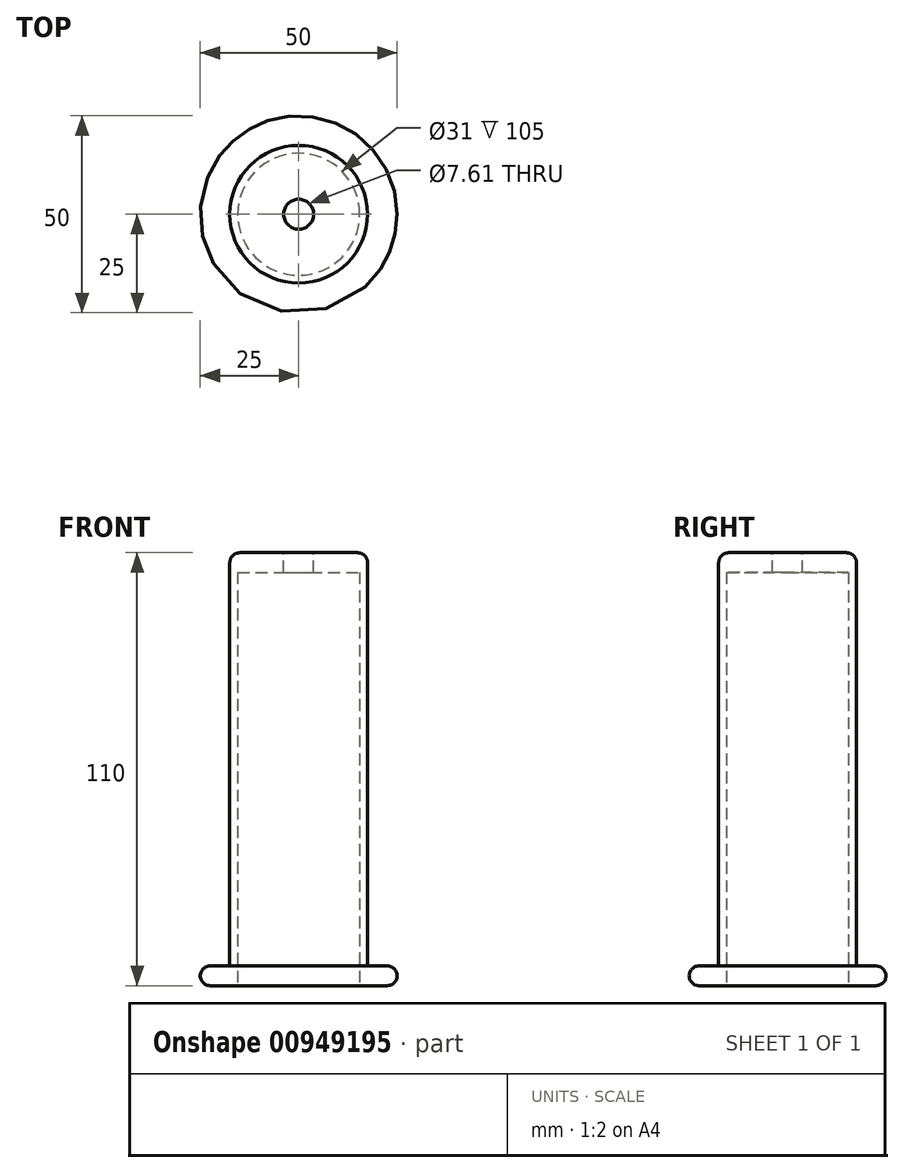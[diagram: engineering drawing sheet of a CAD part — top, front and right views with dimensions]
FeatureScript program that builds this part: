
annotation { "Feature Type Name" : "Feature", "Feature Type Description" : "" }
export const myFeature = defineFeature(function(context is Context, id is Id, definition is map)
    precondition{}
    {
        {
            var Q0;
            Q0=qCreatedBy(makeId("Top.planeOp"),FACE);
            var sketch = newSketch(context, id + "F0", { "sketchPlane" : qUnion([Q0])});
            skCircle(sketch, "E0", {"center": v(0, 0) * mm, "radius": 25 * mm});
            skSolve(sketch);
        }
        {
            var Q0;
            Q0 = qSketchRegion(id + "F0", true);
            var Q1;
            Q1=makeQuery(id+"F0.imprint","IMPRINT",FACE,{"disambiguationData":[TD([[makeQuery(id+"F0.imprint","IMPRINT",EDGE,{"derivedFrom":sQuery(id+"F0.wireOp",EDGE,"E0")}),1.0]])]});
            extrude(context, id + "F1", {"entities" : qUnion([Q0, Q1]), "depth" : 5 * mm, "offsetDistance" : 25 * mm});
        }
        {
            var Q0;
            Q0=makeQuery(id+"F1.opExtrude","CAP_FACE",FACE,{"disambiguationData":[OSD([sQuery(id+"F0.wireOp",EDGE,"E0")])],"isStart":false});
            var sketch = newSketch(context, id + "F2", { "sketchPlane" : qUnion([Q0])});
            skCircle(sketch, "E1", {"center": v(0, 0) * mm, "radius": 17.5 * mm});
            skSolve(sketch);
        }
        {
            var Q0;
            Q0 = qSketchRegion(id + "F2", true);
            var Q1;
            Q1=makeQuery(id+"F2.imprint","IMPRINT",FACE,{"disambiguationData":[TD([[makeQuery(id+"F2.imprint","IMPRINT",EDGE,{"derivedFrom":sQuery(id+"F2.wireOp",EDGE,"E1")}),1.0]])]});
            extrude(context, id + "F3", {"entities" : qUnion([Q0, Q1]), "operationType" : NewBodyOperationType.ADD, "depth" : 105 * mm, "offsetDistance" : 25 * mm});
        }
        {
            var Q0;
            Q0=makeQuery(id+"F1.opExtrude","CAP_FACE",FACE,{"disambiguationData":[OSD([sQuery(id+"F0.wireOp",EDGE,"E0")])],"isStart":true});
            var sketch = newSketch(context, id + "F4", { "sketchPlane" : qUnion([Q0])});
            skCircle(sketch, "E2", {"center": v(0, 0) * mm, "radius": 15.5 * mm});
            skSolve(sketch);
        }
        {
            var Q0;
            Q0=makeQuery(id+"F4.imprint","IMPRINT",FACE,{"disambiguationData":[TD([[makeQuery(id+"F4.imprint","IMPRINT",EDGE,{"derivedFrom":sQuery(id+"F4.wireOp",EDGE,"E2")}),1.0]])]});
            extrude(context, id + "F5", {"entities" : qUnion([Q0]), "operationType" : NewBodyOperationType.REMOVE, "oppositeDirection" : true, "depth" : 105 * mm, "offsetDistance" : 25 * mm});
        }
        {
            var Q0;
            Q0=makeQuery(id+"F3.opExtrude","CAP_EDGE",EDGE,{"disambiguationData":[OSD([sQuery(id+"F2.wireOp",EDGE,"E1")])],"isStart":false});
            var Q1;
            Q1=makeQuery(id+"F3.opExtrude","CAP_EDGE",EDGE,{"disambiguationData":[OSD([sQuery(id+"F2.wireOp",EDGE,"E1")])],"isStart":true});
            var Q2;
            Q2=makeQuery(id+"F1.opExtrude","CAP_EDGE",EDGE,{"disambiguationData":[OSD([sQuery(id+"F0.wireOp",EDGE,"E0")])],"isStart":false});
            var Q3;
            Q3=makeQuery(id+"F1.opExtrude","CAP_EDGE",EDGE,{"disambiguationData":[OSD([sQuery(id+"F0.wireOp",EDGE,"E0")])],"isStart":true});
            fillet(context, id + "F6", {"entities" : qUnion([Q0, Q1, Q2, Q3]), "radius" : 2.5 * mm, "tangentPropagation" : true, "allowEdgeOverflow" : false});
        }
        {
            var Q0;
            Q0=makeQuery(id+"F3.opExtrude","CAP_FACE",FACE,{"disambiguationData":[OSD([sQuery(id+"F2.wireOp",EDGE,"E1")])],"isStart":false});
            var sketch = newSketch(context, id + "F7", { "sketchPlane" : qUnion([Q0])});
            skCircle(sketch, "E3", {"center": v(0, 0) * mm, "radius": 3.8 * mm});
            skSolve(sketch);
        }
        {
            var Q0;
            Q0=makeQuery(id+"F7.imprint","IMPRINT",FACE,{"disambiguationData":[TD([[makeQuery(id+"F7.imprint","IMPRINT",EDGE,{"derivedFrom":sQuery(id+"F7.wireOp",EDGE,"E3")}),1.0]])]});
            extrude(context, id + "F8", {"entities" : qUnion([Q0]), "operationType" : NewBodyOperationType.REMOVE, "oppositeDirection" : true, "depth" : 30 * mm, "offsetDistance" : 25 * mm});
        }
    });
